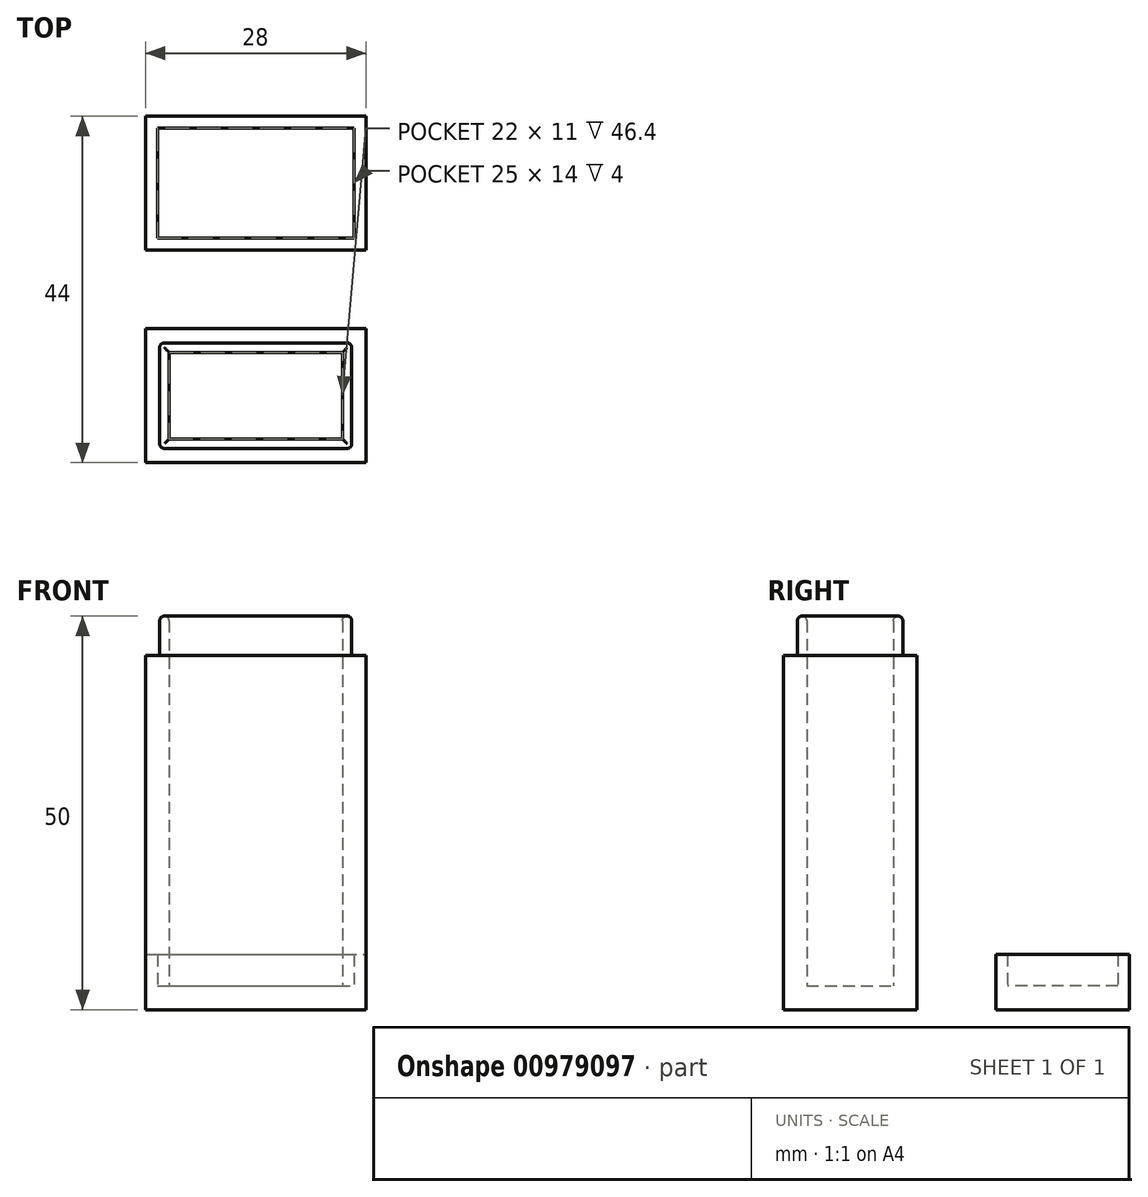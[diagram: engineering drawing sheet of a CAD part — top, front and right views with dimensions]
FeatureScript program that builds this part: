
annotation { "Feature Type Name" : "Feature", "Feature Type Description" : "" }
export const myFeature = defineFeature(function(context is Context, id is Id, definition is map)
    precondition{}
    {
        {
            var Q0;
            Q0=qCreatedBy(makeId("Top.planeOp"),FACE);
            var sketch = newSketch(context, id + "F0", { "sketchPlane" : qUnion([Q0])});
            skLineSegment(sketch, "E0.bottom", {"start": v(0, 0) * mm, "end": v(28, 0) * mm});
            skLineSegment(sketch, "E0.top", {"start": v(0, 17) * mm, "end": v(28, 17) * mm});
            skLineSegment(sketch, "E0.left", {"start": v(0, 0) * mm, "end": v(0, 17) * mm});
            skLineSegment(sketch, "E0.right", {"start": v(28, 0) * mm, "end": v(28, 17) * mm});
            skLineSegment(sketch, "E1.bottom", {"start": v(3, 3) * mm, "end": v(25, 3) * mm});
            skLineSegment(sketch, "E1.top", {"start": v(3, 14) * mm, "end": v(25, 14) * mm});
            skLineSegment(sketch, "E1.left", {"start": v(3, 3) * mm, "end": v(3, 14) * mm});
            skLineSegment(sketch, "E1.right", {"start": v(25, 3) * mm, "end": v(25, 14) * mm});
            skLineSegment(sketch, "E2", {"start": v(0, -10) * mm, "end": v(3, -10) * mm, "construction": true});
            skLineSegment(sketch, "E3", {"start": v(0, 0) * mm, "end": v(0, -10) * mm, "construction": true});
            skLineSegment(sketch, "E4", {"start": v(0, 0) * mm, "end": v(-10, 0) * mm, "construction": true});
            skLineSegment(sketch, "E5", {"start": v(-10, 0) * mm, "end": v(-10, 3) * mm, "construction": true});
            skLineSegment(sketch, "E6", {"start": v(-10, 3) * mm, "end": v(-10, 14) * mm, "construction": true});
            skLineSegment(sketch, "E7", {"start": v(-10, 14) * mm, "end": v(-10, 17) * mm, "construction": true});
            skLineSegment(sketch, "E8", {"start": v(3, -10) * mm, "end": v(25, -10) * mm, "construction": true});
            skLineSegment(sketch, "E9", {"start": v(25, -10) * mm, "end": v(28, -10) * mm, "construction": true});
            skLineSegment(sketch, "E10", {"start": v(0, 17) * mm, "end": v(0, 27) * mm, "construction": true});
            skLineSegment(sketch, "E11.bottom", {"start": v(0, 27) * mm, "end": v(28, 27) * mm});
            skLineSegment(sketch, "E11.top", {"start": v(0, 44) * mm, "end": v(28, 44) * mm});
            skLineSegment(sketch, "E11.left", {"start": v(0, 27) * mm, "end": v(0, 44) * mm});
            skLineSegment(sketch, "E11.right", {"start": v(28, 27) * mm, "end": v(28, 44) * mm});
            skLineSegment(sketch, "E12.bottom", {"start": v(1.5, 42.5) * mm, "end": v(26.5, 42.5) * mm});
            skLineSegment(sketch, "E12.top", {"start": v(1.5, 28.5) * mm, "end": v(26.5, 28.5) * mm});
            skLineSegment(sketch, "E12.left", {"start": v(1.5, 42.5) * mm, "end": v(1.5, 28.5) * mm});
            skLineSegment(sketch, "E12.right", {"start": v(26.5, 42.5) * mm, "end": v(26.5, 28.5) * mm});
            skLineSegment(sketch, "E13", {"start": v(-10, 17) * mm, "end": v(-10, 27) * mm, "construction": true});
            skLineSegment(sketch, "E14", {"start": v(-10, 27) * mm, "end": v(-10, 28.5) * mm, "construction": true});
            skLineSegment(sketch, "E15", {"start": v(-10, 28.5) * mm, "end": v(-10, 42.5) * mm, "construction": true});
            skLineSegment(sketch, "E16", {"start": v(-10, 42.5) * mm, "end": v(-10, 44) * mm, "construction": true});
            skLineSegment(sketch, "E17", {"start": v(-10, 44) * mm, "end": v(-10, 54) * mm, "construction": true});
            skLineSegment(sketch, "E18", {"start": v(-10, 54) * mm, "end": v(0, 54) * mm, "construction": true});
            skLineSegment(sketch, "E19", {"start": v(0, 54) * mm, "end": v(1.5, 54) * mm, "construction": true});
            skLineSegment(sketch, "E20", {"start": v(1.5, 54) * mm, "end": v(26.5, 54) * mm, "construction": true});
            skLineSegment(sketch, "E21", {"start": v(26.5, 54) * mm, "end": v(28, 54) * mm, "construction": true});
            skLineSegment(sketch, "E22.bottom", {"start": v(1.8, 1.8) * mm, "end": v(26.2, 1.8) * mm});
            skLineSegment(sketch, "E22.top", {"start": v(1.8, 15.2) * mm, "end": v(26.2, 15.2) * mm});
            skLineSegment(sketch, "E22.left", {"start": v(1.8, 1.8) * mm, "end": v(1.8, 15.2) * mm});
            skLineSegment(sketch, "E22.right", {"start": v(26.2, 1.8) * mm, "end": v(26.2, 15.2) * mm});
            skLineSegment(sketch, "E23", {"start": v(0, -5) * mm, "end": v(1.8, -5) * mm, "construction": true});
            skLineSegment(sketch, "E24", {"start": v(1.8, -5) * mm, "end": v(26.2, -5) * mm, "construction": true});
            skLineSegment(sketch, "E25", {"start": v(26.2, -5) * mm, "end": v(28, -5) * mm, "construction": true});
            skLineSegment(sketch, "E26", {"start": v(-5, 0) * mm, "end": v(-5, 1.8) * mm, "construction": true});
            skLineSegment(sketch, "E27", {"start": v(-5, 1.8) * mm, "end": v(-5, 15.2) * mm, "construction": true});
            skLineSegment(sketch, "E28", {"start": v(-5, 15.2) * mm, "end": v(-5, 17) * mm, "construction": true});
            skSolve(sketch);
        }
        {
            var Q0;
            Q0=makeQuery(id+"F0.imprint","IMPRINT",FACE,{"disambiguationData":[TD([[makeQuery(id+"F0.imprint","IMPRINT",EDGE,{"derivedFrom":sQuery(id+"F0.wireOp",EDGE,"E1.bottom")}),1.0]])]});
            var Q1;
            Q1=makeQuery(id+"F0.imprint","IMPRINT",FACE,{"disambiguationData":[TD([[makeQuery(id+"F0.imprint","IMPRINT",EDGE,{"derivedFrom":sQuery(id+"F0.wireOp",EDGE,"E12.bottom")}),-1.0]])]});
            extrude(context, id + "F1", {"entities" : qUnion([Q0, Q1]), "depth" : 3 * mm, "offsetDistance" : 25 * mm});
        }
        {
            var Q0;
            Q0=makeQuery(id+"F0.imprint","IMPRINT",FACE,{"disambiguationData":[TD([[makeQuery(id+"F0.imprint","IMPRINT",EDGE,{"derivedFrom":sQuery(id+"F0.wireOp",EDGE,"E1.bottom")}),-1.0]])]});
            extrude(context, id + "F2", {"entities" : qUnion([Q0]), "operationType" : NewBodyOperationType.ADD, "depth" : 50 * mm, "offsetDistance" : 25 * mm});
        }
        {
            var Q0;
            Q0=makeQuery(id+"F0.imprint","IMPRINT",FACE,{"disambiguationData":[TD([[makeQuery(id+"F0.imprint","IMPRINT",EDGE,{"derivedFrom":sQuery(id+"F0.wireOp",EDGE,"E0.bottom")}),1.0]])]});
            extrude(context, id + "F3", {"entities" : qUnion([Q0]), "operationType" : NewBodyOperationType.ADD, "depth" : 45 * mm, "offsetDistance" : 25 * mm});
        }
        {
            var Q0;
            Q0=makeQuery(id+"F0.imprint","IMPRINT",FACE,{"disambiguationData":[TD([[makeQuery(id+"F0.imprint","IMPRINT",EDGE,{"derivedFrom":sQuery(id+"F0.wireOp",EDGE,"E11.bottom")}),1.0]])]});
            extrude(context, id + "F4", {"entities" : qUnion([Q0]), "operationType" : NewBodyOperationType.ADD, "depth" : 7 * mm, "offsetDistance" : 25 * mm});
        }
        {
            var Q0;
            Q0=makeQuery(id+"F2.opExtrude","CAP_FACE",FACE,{"disambiguationData":[OSD([sQuery(id+"F0.wireOp",EDGE,"E1.bottom"),sQuery(id+"F0.wireOp",EDGE,"E1.top"),sQuery(id+"F0.wireOp",EDGE,"E1.left"),sQuery(id+"F0.wireOp",EDGE,"E1.right"),sQuery(id+"F0.wireOp",EDGE,"E22.bottom"),sQuery(id+"F0.wireOp",EDGE,"E22.top"),sQuery(id+"F0.wireOp",EDGE,"E22.left"),sQuery(id+"F0.wireOp",EDGE,"E22.right")])],"isStart":false});
            var Q1;
            Q1=makeQuery(id+"F2.opExtrude","SWEPT_EDGE",EDGE,{"disambiguationData":[OSD([sQuery(id+"F0.wireOp",EDGE,"E22.bottom"),sQuery(id+"F0.wireOp",EDGE,"E22.right")])]});
            var Q2;
            Q2=makeQuery(id+"F2.opExtrude","SWEPT_EDGE",EDGE,{"disambiguationData":[OSD([sQuery(id+"F0.wireOp",EDGE,"E22.top"),sQuery(id+"F0.wireOp",EDGE,"E22.right")])]});
            var Q3;
            Q3=makeQuery(id+"F2.opExtrude","SWEPT_EDGE",EDGE,{"disambiguationData":[OSD([sQuery(id+"F0.wireOp",EDGE,"E22.top"),sQuery(id+"F0.wireOp",EDGE,"E22.left")])]});
            var Q4;
            Q4=makeQuery(id+"F2.opExtrude","SWEPT_EDGE",EDGE,{"disambiguationData":[OSD([sQuery(id+"F0.wireOp",EDGE,"E22.bottom"),sQuery(id+"F0.wireOp",EDGE,"E22.left")])]});
            fillet(context, id + "F5", {"entities" : qUnion([Q0, Q1, Q2, Q3, Q4]), "radius" : .6 * mm, "tangentPropagation" : true, "allowEdgeOverflow" : false});
        }
    });
